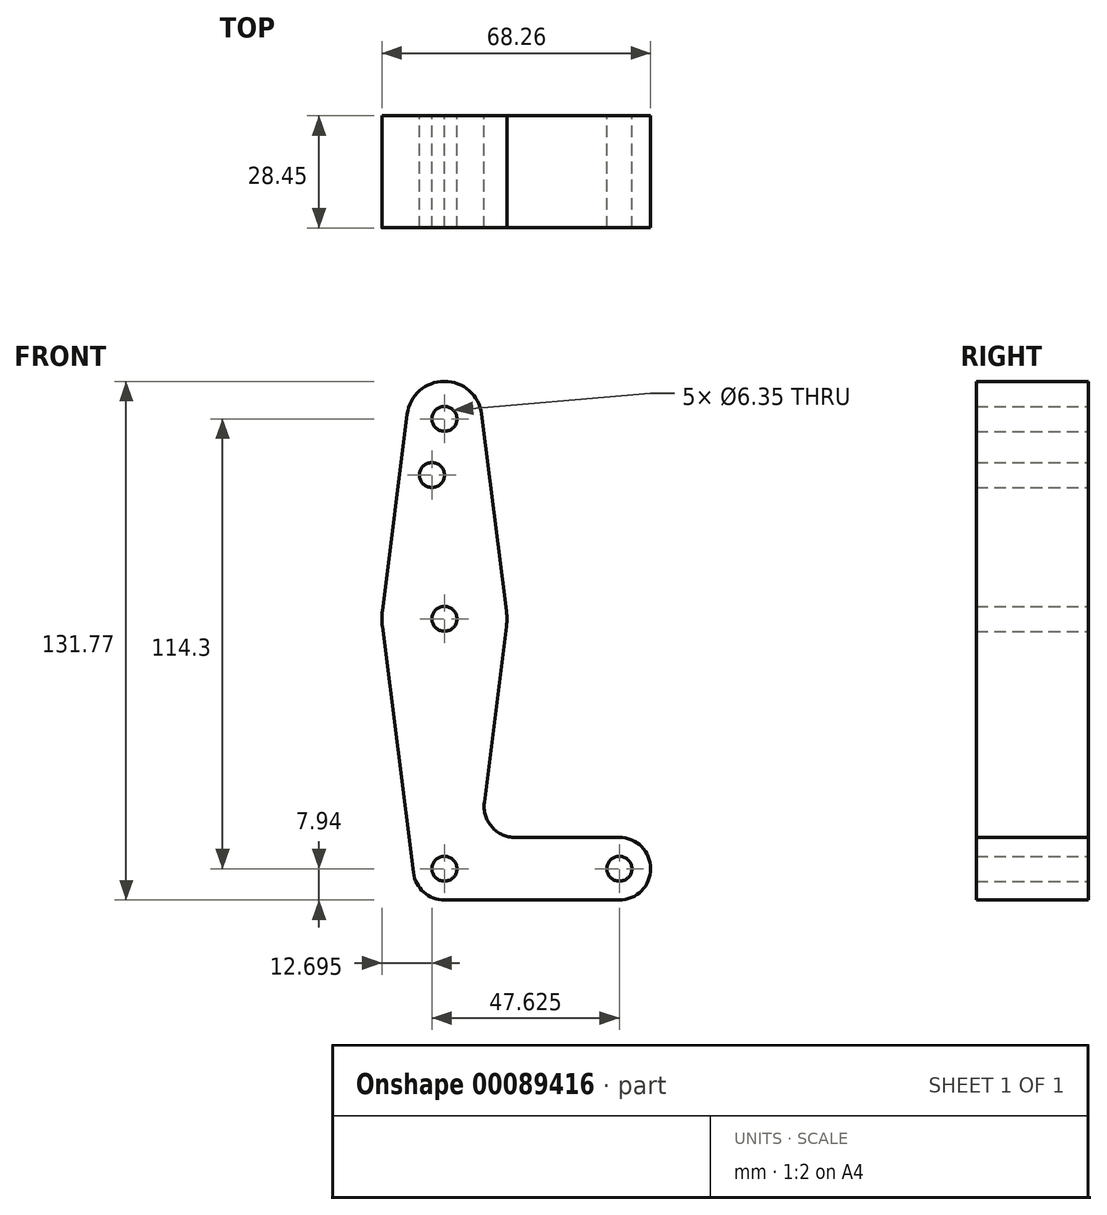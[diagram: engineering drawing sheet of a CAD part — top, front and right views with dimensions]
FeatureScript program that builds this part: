
annotation { "Feature Type Name" : "Feature", "Feature Type Description" : "" }
export const myFeature = defineFeature(function(context is Context, id is Id, definition is map)
    precondition{}
    {
        {
            var Q0;
            Q0=qCreatedBy(makeId("Front.planeOp"),FACE);
            var sketch = newSketch(context, id + "F0", { "sketchPlane" : qUnion([Q0])});
            skLineSegment(sketch, "E0", {"start": v(0, 114.3) * mm, "end": v(0, 0) * mm});
            skLineSegment(sketch, "E1", {"start": v(0, 0) * mm, "end": v(44.45, 0) * mm});
            skCircle(sketch, "E2", {"center": v(0, 114.3) * mm, "radius": 9.53 * mm});
            skCircle(sketch, "E3", {"center": v(0, 63.5) * mm, "radius": 15.88 * mm});
            skCircle(sketch, "E4", {"center": v(0, 0) * mm, "radius": 7.94 * mm});
            skCircle(sketch, "E5", {"center": v(44.45, 0) * mm, "radius": 7.94 * mm});
            skLineSegment(sketch, "E6", {"start": v(9.45, 115.5) * mm, "end": v(15.75, 65.48) * mm});
            skLineSegment(sketch, "E7", {"start": v(-9.45, 115.5) * mm, "end": v(-15.75, 65.48) * mm});
            skLineSegment(sketch, "E8", {"start": v(15.75, 61.52) * mm, "end": v(10.13, 16.88) * mm});
            skLineSegment(sketch, "E9", {"start": v(18.01, 7.94) * mm, "end": v(44.45, 7.94) * mm});
            skLineSegment(sketch, "E10", {"start": v(0, -7.94) * mm, "end": v(44.45, -7.94) * mm});
            skCircle(sketch, "E11", {"center": v(0, 114.3) * mm, "radius": 3.18 * mm});
            skCircle(sketch, "E12", {"center": v(0, 63.5) * mm, "radius": 3.18 * mm});
            skCircle(sketch, "E13", {"center": v(0, 0) * mm, "radius": 3.18 * mm});
            skCircle(sketch, "E14", {"center": v(44.45, 0) * mm, "radius": 3.18 * mm});
            skCircle(sketch, "E15", {"center": v(-3.18, 100.03) * mm, "radius": 3.18 * mm});
            skArc(sketch, "E16.filletArc", {"start": v(10.13, 16.88) * mm, "mid": v(12.05, 10.63) * mm, "end": v(18.01, 7.94) * mm});
            skLineSegment(sketch, "E17", {"start": v(-15.75, 61.52) * mm, "end": v(-7.88, -1) * mm});
            skSolve(sketch);
        }
        {
            var Q0;
            Q0 = qSketchRegion(id + "F0", true);
            extrude(context, id + "F1", {"entities" : qUnion([Q0]), "depth" : 3.05 * mm});
        }
        {
            var Q0;
            Q0 = qSketchRegion(id + "F0", true);
            extrude(context, id + "F2", {"entities" : qUnion([Q0]), "operationType" : NewBodyOperationType.ADD, "depth" : 3.05 * mm});
        }
        {
            var Q0;
            {var subQ0=sQuery(id+"F0.wireOp",EDGE,"E4");var subQ1=sQuery(id+"F0.wireOp",EDGE,"E0");var subQ2=makeQuery(id+"F0.imprint","INTERSECT",VERTEX,{"derivedFrom":[subQ1,subQ0]});Q0=makeQuery(id+"F0.imprint","IMPRINT",FACE,{"disambiguationData":[TD([[makeQuery(id+"F0.imprint","IMPRINT",EDGE,{"disambiguationData":[TD([[subQ2,-1.0]])],"derivedFrom":subQ1}),1.0]])]});}
            var Q1;
            {var subQ3=sQuery(id+"F0.wireOp",EDGE,"E4");var subQ7=sQuery(id+"F0.wireOp",EDGE,"E0");var subQ8=makeQuery(id+"F0.imprint","INTERSECT",VERTEX,{"derivedFrom":[subQ7,subQ3]});Q1=makeQuery(id+"F0.imprint","IMPRINT",FACE,{"disambiguationData":[TD([[makeQuery(id+"F0.imprint","IMPRINT",EDGE,{"disambiguationData":[TD([[subQ8,-1.0]])],"derivedFrom":subQ7}),-1.0]])]});}
            var Q2;
            Q2=makeQuery(id+"F1.opExtrude","CAP_FACE",FACE,{"disambiguationData":[OSD([sQuery(id+"F0.wireOp",EDGE,"E0"),sQuery(id+"F0.wireOp",EDGE,"E1"),sQuery(id+"F0.wireOp",EDGE,"E2"),sQuery(id+"F0.wireOp",EDGE,"E3"),sQuery(id+"F0.wireOp",EDGE,"E4"),sQuery(id+"F0.wireOp",EDGE,"E5"),sQuery(id+"F0.wireOp",EDGE,"E6"),sQuery(id+"F0.wireOp",EDGE,"E7"),sQuery(id+"F0.wireOp",EDGE,"E8"),sQuery(id+"F0.wireOp",EDGE,"E9"),sQuery(id+"F0.wireOp",EDGE,"E10"),sQuery(id+"F0.wireOp",EDGE,"E11"),sQuery(id+"F0.wireOp",EDGE,"E12"),sQuery(id+"F0.wireOp",EDGE,"E13"),sQuery(id+"F0.wireOp",EDGE,"E14"),sQuery(id+"F0.wireOp",EDGE,"E15"),sQuery(id+"F0.wireOp",EDGE,"E16.filletArc"),sQuery(id+"F0.wireOp",EDGE,"E17")])],"isStart":false});
            extrude(context, id + "F3", {"entities" : qUnion([Q0, Q1, Q2]), "operationType" : NewBodyOperationType.ADD, "depth" : 25.4 * mm});
        }
        {
            var Q0;
            Q0 = qSketchRegion(id + "F0", true);
            var Q1;
            Q1=makeQuery(id+"F3.opExtrude","CAP_FACE",FACE,{"disambiguationData":[OSD([sQuery(id+"F0.wireOp",EDGE,"E4"),sQuery(id+"F0.wireOp",EDGE,"E13")])],"isStart":false});
            extrude(context, id + "F4", {"entities" : qUnion([Q0, Q1]), "operationType" : NewBodyOperationType.ADD, "depth" : 3.05 * mm});
        }
    });
